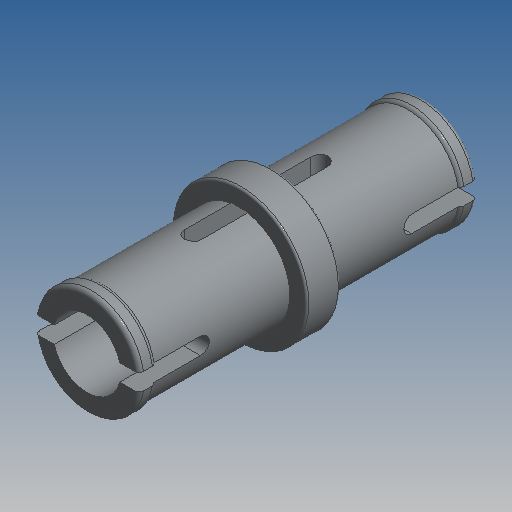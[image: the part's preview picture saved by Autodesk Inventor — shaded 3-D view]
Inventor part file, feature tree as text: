
AUTODESK INVENTOR PART (.ipt)
format: ipt  version: 2022.2 (Build 262287000, 287)  size: 294,912 bytes
history: native  units: mm (DEFAULTED — no unit token found)
features: sketch x2, extrude x2, revolve x1, fillet x1
ambient origin geometry x8: Origin, YZ Plane, XZ Plane, XY Plane, X Axis, Y Axis, Z Axis, Center Point
bodies: Solid2 (feature_tree)
feature tree (6):
  sketch  "Sketch1"  dims[d1=4.8mm d2=5.0mm d6=8.0mm]
  revolve  "Revolution1"  [1 undecoded]
  fillet  "Fillet1"  Radius=8.0mm
  extrude  "Extrusion1"  Depth=10.0mm
  extrude  "Extrusion2"  Depth=0.8mm
  sketch  "Sketch2"  dims[d7=0.8mm d8=6.4mm d9=0.8mm d10=0.8mm d14=0.8mm d19=8.0mm d20=90.0deg d21=4.8mm d22=0.0mm d24=0.8mm d25=10.0mm d26=0.0mm d27=0.2mm d28=0.1mm d29=0.0mm d30=0.0mm d31=3.4mm d32=3.2mm d33=3.4mm]
note: 1 required parameter value undecoded (feature->parameter linkage not recoverable at this tier; creation-order binding heuristic only, values carry confidence <= 0.55)
